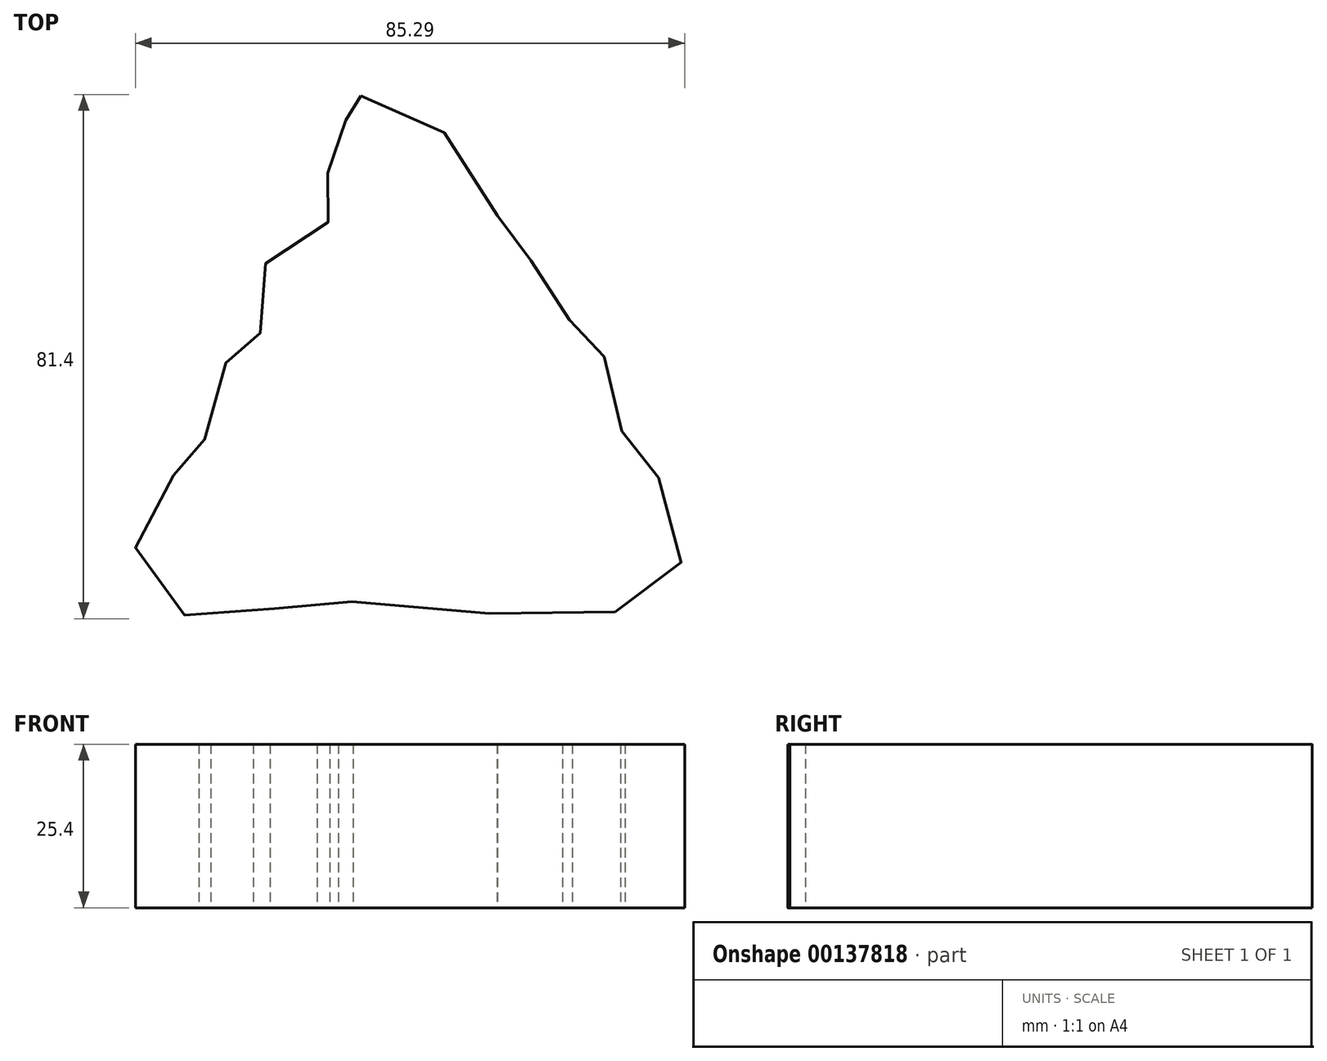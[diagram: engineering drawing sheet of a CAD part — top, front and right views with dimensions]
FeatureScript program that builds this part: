
annotation { "Feature Type Name" : "Feature", "Feature Type Description" : "" }
export const myFeature = defineFeature(function(context is Context, id is Id, definition is map)
    precondition{}
    {
        {
            var Q0;
            Q0=qCreatedBy(makeId("Top.planeOp"),FACE);
            var sketch = newSketch(context, id + "F0", { "sketchPlane" : qUnion([Q0])});
            skPoint(sketch, "E0.18.internal.orphan", {"position": v(39.05, 0) * mm});
            skPoint(sketch, "E0.41.internal.orphan", {"position": v(-25.76, 0) * mm});
            skPoint(sketch, "E0.6.internal.orphan", {"position": v(0, 44.58) * mm});
            skFitSpline(sketch, "E1", {"points": [v(-1.81, 44.58) * mm, v(8.45, 40.56) * mm, v(19.12, 29.09) * mm, v(19.93, 20.43) * mm, v(26.37, 18.42) * mm, v(31, 11.17) * mm, v(29.59, 6.94) * mm, v(36.83, 3.52) * mm, v(39.05, -5.33) * mm, v(39.05, -11.37) * mm, v(45.49, -15.6) * mm, v(48.1, -27.27) * mm, v(41.67, -34.32) * mm, v(23.55, -36.13) * mm, v(-4.03, -33.92) * mm, v(-12.28, -34.32) * mm, v(-23.35, -36.53) * mm, v(-33.61, -33.51) * mm, v(-36.63, -22.44) * mm, v(-31, -14.4) * mm, v(-25.16, -11.57) * mm, v(-26.57, -7.35) * mm, v(-23.75, 2.52) * mm, v(-15.9, 5.74) * mm, v(-17.91, 8.55) * mm, v(-17.51, 16.6) * mm, v(-13.49, 21.44) * mm, v(-6.64, 25.46) * mm, v(-8.45, 28.08) * mm, v(-5.64, 34.32) * mm, v(-3.02, 38.55) * mm, v(-5.23, 42.77) * mm, v(-4.43, 44.58) * mm, v(-1.81, 44.58) * mm]});
            skSolve(sketch);
        }
        {
            var Q0;
            Q0=makeQuery(id+"F0.imprint","IMPRINT",FACE,{"disambiguationData":[TD([[makeQuery(id+"F0.imprint","IMPRINT",EDGE,{"derivedFrom":sQuery(id+"F0.wireOp",EDGE,"E1")}),-1.0]])]});
            extrude(context, id + "F1", {"entities" : qUnion([Q0]), "depth" : 25.4 * mm});
        }
    });
